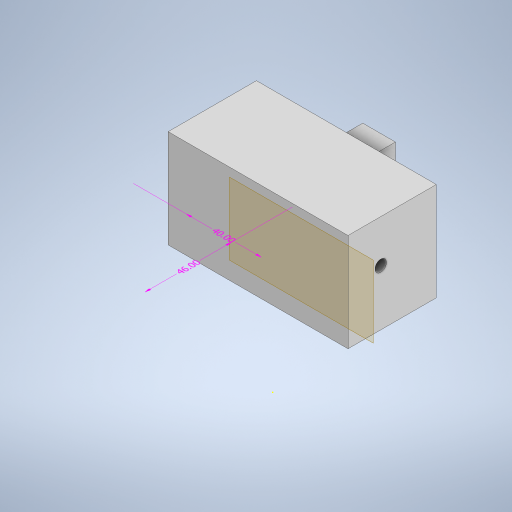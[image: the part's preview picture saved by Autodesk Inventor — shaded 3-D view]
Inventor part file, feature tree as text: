
AUTODESK INVENTOR PART (.ipt)
format: ipt  version: 2023 (Build 270158000, 158)  size: 303,616 bytes
history: native  units: mm
features: sketch x8, extrude x6, other x4, plane x3, hole x1, split x1
ambient origin geometry x8: Origin, YZ Plane, XZ Plane, XY Plane, X Axis, Y Axis, Z Axis, Center Point
bodies: Body1 (feature_tree)
feature tree (23):
  other  "Sólido1"
  other  "Anotaciones"
  extrude  "Extrusión1"  Depth=55.0mm
  extrude  "Extrusión2"  Depth=10.0mm
  extrude  "Extrusión3"  Depth=5.0mm
  extrude  "Extrusión4"  Depth=10.0mm TaperAngle=0.0deg
  plane  "Plano de trabajo1"
  extrude  "Extrusión5"  Depth=10.0mm
  plane  "Plano de trabajo2"
  extrude  "Extrusión6"  Depth=40.0mm
  sketch  "Boceto7"  dims[d15=46.0mm d16=20.0mm d17=0.0mm]
  plane  "Plano de trabajo4"
  hole  "Agujero1"  [1 undecoded]
  split  "Dividir1"
  sketch  "Boceto1"  dims[d0=55.0mm d1=100.0mm]
  sketch  "Boceto2"  dims[d2=30.0mm d3=0.0mm d4=10.0mm]
  sketch  "Boceto3"  dims[d5=20.0mm d6=5.0mm]
  sketch  "Boceto4"  dims[d7=22.5mm d8=10.0mm d9=0.0mm]
  sketch  "Boceto5"  dims[d10=10.0mm d11=10.0mm]
  sketch  "Boceto6"  dims[d12=15.0mm d13=0.0mm d14=40.0mm]
  sketch  "Boceto8"  dims[d24=22.5mm d25=2.5mm d26=2.5mm d27=8.0mm d28=0.0mm d29=3.0mm d30=3.0mm d31=8.0mm d32=0.0mm d33=0.0mm d34=10.0mm d35=30.0mm d36=5.0mm d37=5.0mm d38=5.0mm d39=5.0mm d40=10.0mm d41=8.0mm d42=3.5mm d43=6.0mm d44=4.0mm d45=2.0mm d46=90.0deg d47=8.0mm d48=20.594885mm d18=5.462798mm d19=4.90751mm d20=46.0mm d21=4.68859mm d22=6.124374mm d23=40.0mm]
  other  "Cota lineal 1"
  other  "Cota lineal 2"
note: 1 required parameter value undecoded (feature->parameter linkage not recoverable at this tier; creation-order binding heuristic only, values carry confidence <= 0.55)
